# Revit family: 90 KISS PIVOT HEAVY DUTY HINGED DOOR WITH TRANSOM)
name_source: partatom
category: Generic Models
revit_build: Autodesk Revit 2018 (Build: 20190510_1515(x64)
units: mm (PartAtom-declared; Revit-internal decimal feet)

## family parameters
Always vertical = Yes
Can host rebar = No
Cut with Voids When Loaded = No
Part Type = Normal
Room Calculation Point = No
Round Connector Dimension = Use Diameter
Shared = No
Work Plane-Based = No

## types (1)
- 90 KISS PIVOT HEAVY DUTY HINGED DOOR WITH TRANSOM)
    ACTUAL NUMBER OF BOTTOM BLADES LIMITS = 10
    ACTUAL NUMBER OF TOP BLADES LIMITS = 17
    BLADE SPACING = 80 mm  [stored 0.262467 ft]
    BOTTOM BLADES = 10
    BOTTOM BLADES INFO = MIN BLADES (9), MAX BLADES (10),  IDEALLY WANT TRANSOM HEIGHT @ (1000)
    DOOR ANGLE = 0.00°
    FRAME = <By Category>
    HEIGHT INPUT = 2500 mm  [stored 8.2021 ft]
    HINGE DOOR ANGLE LIMITS = 0.00°
    LOUVRE BLADE ANGLE = 0.00°
    MODULE PANEL HEIGHT = 2500 mm  [stored 8.2021 ft]
    OVERALL HEIGHT = 2530 mm
    OVERALL WIDTH = 1060 mm
    OVERALL WIDTH LIMITS = 1060 mm
    PANEL HEIGHT INFO = PANELS ARE AVAILABLE IN VARIOUS MODULE SIZES. IF YOU NEED A SPECIFIC HEIGHT, RIPPED BLADES MAY BE REQUIRED. PLEASE CONTACT THE LOUVRETEC TEAM OR VISIT OUR WEBSITE FOR ASSISTANCE.
PANELS ARE AVAILABLE IN VARIOUS MODULE SIZES. IF YOU NEED A SPECIFIC HEIGHT, RIPPED BLADES MAY BE REQUIRED. PLEASE CONTACT THE LOUVRETEC TEAM OR VISIT OUR WEBSITE FOR ASSISTANCE.
    PANEL WIDTH = 1000 mm  [stored 3.28084 ft]
    PANEL WIDTH INFO = PANEL TYPICAL SIZES  MIN 900, MAX 1200
    TOP BLADES = 17
    TOP BLADES INFO = MIN BLADES (11), MAX BLADES (18)
    WEBSITE = https://louvretec.co.nz
    WIDTH INPUT = 1000 mm  [stored 3.28084 ft]
    WIDTH REMAINDER = 60 mm  [stored 0.19685 ft]

note: [stored X ft] marks values corroborated as IEEE doubles in the binary element streams (Revit-internal decimal feet)

## geometry (parser evidence)
native form markers: Sweep x62
no freeform markers — native parametric forms only
